FCSTD DOCUMENT  (FreeCAD 0.14R3702 (Git))
Label: Modelodelgabinete3
License: CC-BY 3.0
LicenseURL: http://creativecommons.org/licenses/by/3.0/
objects: Sketcher::SketchObject×1
note: 1 computed .brp shape members not serialized (recipe doc carries the construction recipe); baked Part::Feature solids carry a one-line shape summary decoded from their .brp

FEATURE [Sketcher::SketchObject] Sketch
  sketch-geometry (19):
    g0: LineSegment [constr] StartX=-56.1975 StartY=40.005 StartZ=0 EndX=56.1975 EndY=40.005 EndZ=0
    g1: LineSegment [constr] StartX=56.1975 StartY=40.005 StartZ=0 EndX=56.1975 EndY=-40.005 EndZ=0
    g2: LineSegment [constr] StartX=56.1975 StartY=-40.005 StartZ=0 EndX=-56.1975 EndY=-40.005 EndZ=0
    g3: LineSegment [constr] StartX=-56.1975 StartY=-40.005 StartZ=0 EndX=-56.1975 EndY=40.005 EndZ=0
    g4: Circle [constr] CenterX=-41.5925 CenterY=36.195 CenterZ=0 NormalX=0 NormalY=0 NormalZ=1 Radius=1.5
    g5: LineSegment [constr] StartX=-41.5925 StartY=36.195 StartZ=0 EndX=44.7675 EndY=36.195 EndZ=0
    g6: Circle [constr] CenterX=44.7675 CenterY=36.195 CenterZ=0 NormalX=0 NormalY=0 NormalZ=1 Radius=1.5
    g7: LineSegment [constr] StartX=44.7675 StartY=36.195 StartZ=0 EndX=44.7675 EndY=-11.43 EndZ=0
    g8: Circle [constr] CenterX=44.7675 CenterY=-11.43 CenterZ=0 NormalX=0 NormalY=0 NormalZ=1 Radius=1.5
    g9: LineSegment [constr] StartX=44.7675 StartY=-11.43 StartZ=0 EndX=-41.5925 EndY=-11.43 EndZ=0
    g10: Circle [constr] CenterX=-41.5925 CenterY=-11.43 CenterZ=0 NormalX=0 NormalY=0 NormalZ=1 Radius=1.5
    g11: LineSegment StartX=-58.1975 StartY=42.005 StartZ=0 EndX=58.1975 EndY=42.005 EndZ=0
    g12: LineSegment StartX=58.1975 StartY=42.005 StartZ=0 EndX=58.1975 EndY=-42.005 EndZ=0
    g13: LineSegment StartX=58.1975 StartY=-42.005 StartZ=0 EndX=-58.1975 EndY=-42.005 EndZ=0
    g14: LineSegment StartX=-58.1975 StartY=-42.005 StartZ=0 EndX=-58.1975 EndY=42.005 EndZ=0
    g15: LineSegment StartX=-60.1975 StartY=44.005 StartZ=0 EndX=60.1975 EndY=44.005 EndZ=0
    g16: LineSegment StartX=60.1975 StartY=44.005 StartZ=0 EndX=60.1975 EndY=-44.005 EndZ=0
    g17: LineSegment StartX=60.1975 StartY=-44.005 StartZ=0 EndX=-60.1975 EndY=-44.005 EndZ=0
    g18: LineSegment StartX=-60.1975 StartY=-44.005 StartZ=0 EndX=-60.1975 EndY=44.005 EndZ=0
  constraints (54):
    c: Coincident(g0,g1)
    c: Coincident(g1,g2)
    c: Coincident(g2,g3)
    c: Coincident(g3,g0)
    c: Horizontal(g0)
    c: Horizontal(g2)
    c: Vertical(g1)
    c: Vertical(g3)
    c: DistanceX(g2) = -112.395
    c: DistanceY(g1) = -80.01
    c: Symmetric(g0,g0,g-2)
    c: Symmetric(g0,g2,g-1)
    c: DistanceY(g4,g0) = 3.81
    c: Radius(g4) = 1.5
    c: DistanceX(g0,g4) = 14.605
    c: Coincident(g5,g4)
    c: Horizontal(g5)
    c: DistanceX(g5) = 86.36
    c: Coincident(g6,g5)
    c: Radius(g6) = 1.5
    c: Coincident(g7,g5)
    c: Vertical(g7)
    c: DistanceY(g7) = -47.625
    c: Coincident(g8,g7)
    c: Radius(g8) = 1.5
    c: Coincident(g9,g7)
    c: Horizontal(g9)
    c: Equal(g9,g5)
    c: Coincident(g10,g9)
    c: Radius(g10) = 1.5
    c: Coincident(g11,g12)
    c: Coincident(g12,g13)
    c: Coincident(g13,g14)
    c: Coincident(g14,g11)
    c: Horizontal(g11)
    c: Horizontal(g13)
    c: Vertical(g12)
    c: Vertical(g14)
    c: DistanceY(g0,g11) = 2
    c: DistanceX(g0,g11) = -2
    c: DistanceX(g1,g12) = 2
    c: DistanceY(g12,g1) = 2
    c: Coincident(g15,g16)
    c: Coincident(g16,g17)
    c: Coincident(g17,g18)
    c: Coincident(g18,g15)
    c: Horizontal(g15)
    c: Horizontal(g17)
    c: Vertical(g16)
    c: Vertical(g18)
    c: DistanceY(g11,g15) = 2
    c: DistanceX(g15,g11) = 2
    c: DistanceY(g16,g12) = 2
    c: DistanceX(g16,g12) = -2
